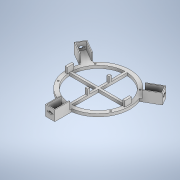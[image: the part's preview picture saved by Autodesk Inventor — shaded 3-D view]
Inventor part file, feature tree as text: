
AUTODESK INVENTOR PART (.ipt)
format: ipt  version: 2020 (Build 240168000, 168)  size: 279,552 bytes
history: native  units: mm
features: extrude x4, sketch x4, pattern_circular x1
ambient origin geometry x8: Origin, YZ Plane, XZ Plane, XY Plane, X Axis, Y Axis, Z Axis, Center Point
bodies: Solid1 (feature_tree)
feature tree (9):
  extrude  "Extrusion1"  Depth=100.0mm
  extrude  "Extrusion4"  Depth=4.0mm
  extrude  "Extrusion5"  Depth=100.0mm
  extrude  "Extrusion6"  Depth=35.0mm
  pattern_circular  "Circular Pattern2"  [2 undecoded]
  sketch  "Sketch1"  dims[d0=114.0mm d1=100.0mm]
  sketch  "Sketch5"  dims[d6=100.0mm d7=4.0mm]
  sketch  "Sketch6"  dims[d8=4.0mm d9=100.0mm]
  sketch  "Sketch7"  dims[d10=17.0mm d14=60.0mm d15=27.0mm d16=30.0mm d18=360.0deg d20=5.0mm d21=0.0mm d41=17.5mm d42=4.0mm d43=12.0mm d44=10.0mm d45=0.0mm d46=27.0mm d47=1.5mm d48=13.5mm d49=0.0mm d50=5.0mm d51=5.0mm d53=9.0mm d54=2.0mm d55=2.0mm d56=13.5mm d57=0.0mm d58=30.0mm d59=360.0deg d61=107.0mm d62=3.0mm d63=3.0mm d64=3.0mm d65=3.0mm d66=35.0mm d67=35.0mm d68=25.0mm d69=25.0mm]
note: 2 required parameter values undecoded (feature->parameter linkage not recoverable at this tier; creation-order binding heuristic only, values carry confidence <= 0.55)
